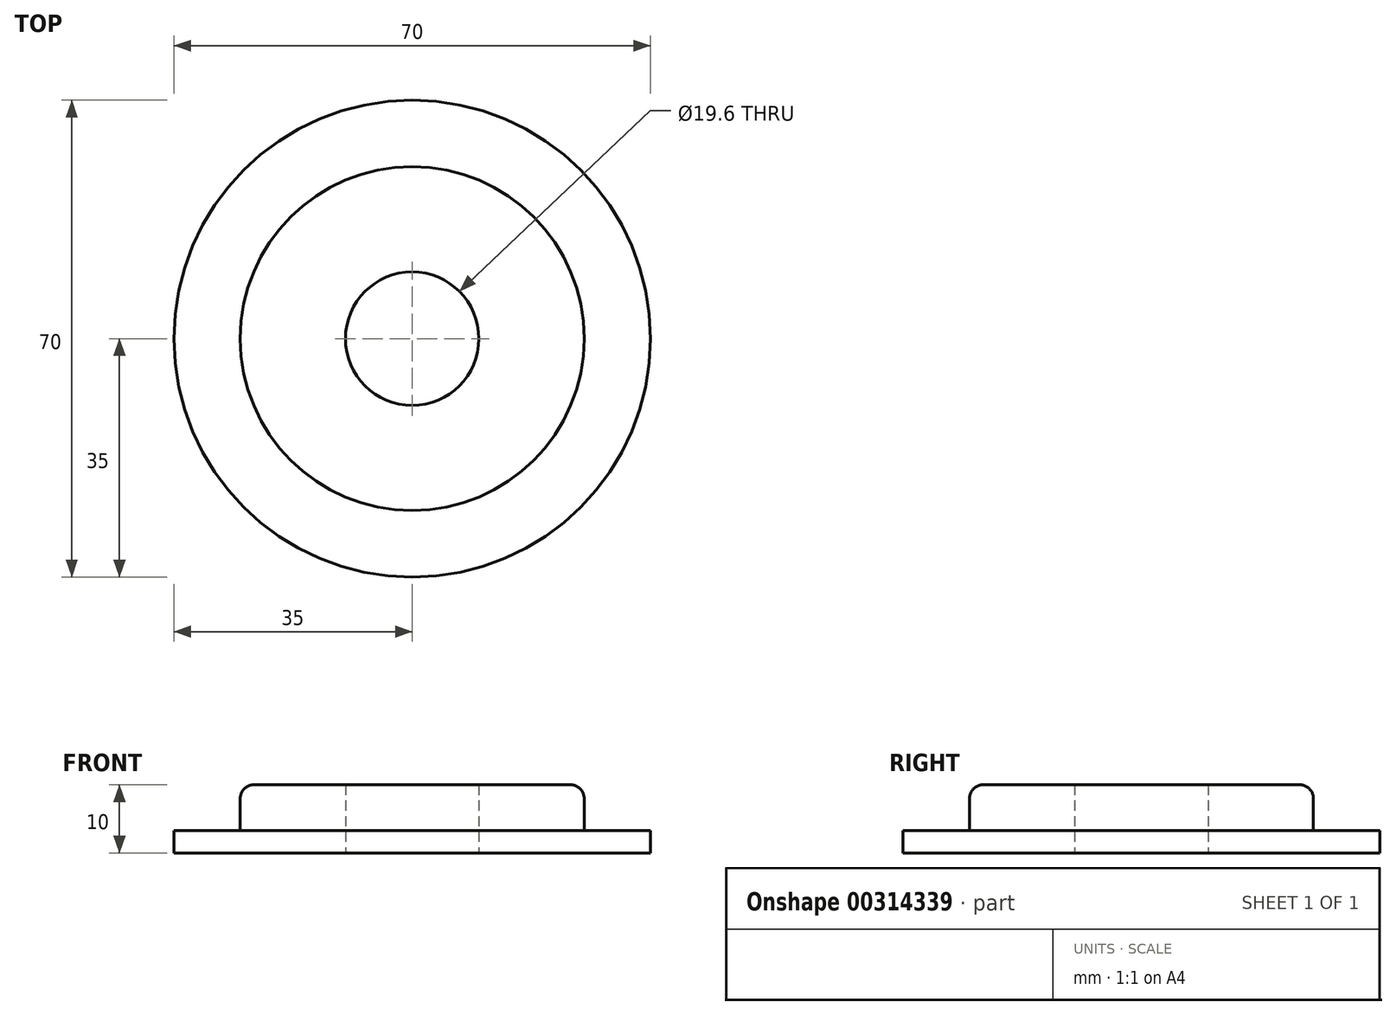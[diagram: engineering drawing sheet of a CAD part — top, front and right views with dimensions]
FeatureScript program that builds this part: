
annotation { "Feature Type Name" : "Feature", "Feature Type Description" : "" }
export const myFeature = defineFeature(function(context is Context, id is Id, definition is map)
    precondition{}
    {
        {
            var Q0;
            Q0=qCreatedBy(makeId("Top.planeOp"),FACE);
            var sketch = newSketch(context, id + "F0", { "sketchPlane" : qUnion([Q0])});
            skCircle(sketch, "E0", {"center": v(0, 0) * mm, "radius": 25.25 * mm});
            skCircle(sketch, "E1", {"center": v(0, 0) * mm, "radius": 9.8 * mm});
            skCircle(sketch, "E2", {"center": v(0, 0) * mm, "radius": 35 * mm});
            skCircle(sketch, "E3", {"center": v(0, 0) * mm, "radius": 12 * mm});
            skCircle(sketch, "E4", {"center": v(0, 0) * mm, "radius": 32 * mm});
            skSolve(sketch);
        }
        {
            var Q0;
            Q0=makeQuery(id+"F0.imprint","IMPRINT",FACE,{"disambiguationData":[TD([[makeQuery(id+"F0.imprint","IMPRINT",EDGE,{"derivedFrom":sQuery(id+"F0.wireOp",EDGE,"E0")}),1.0]])]});
            var Q1;
            Q1=makeQuery(id+"F0.imprint","IMPRINT",FACE,{"disambiguationData":[TD([[makeQuery(id+"F0.imprint","IMPRINT",EDGE,{"derivedFrom":sQuery(id+"F0.wireOp",EDGE,"E1")}),-1.0]])]});
            var Q2;
            {var subQ0=sQuery(id+"F0.wireOp",EDGE,"DjPiPHxe-zXuA-ZsiI-Qa3n-cukn8P3f6TYJ");var subQ1=sQuery(id+"F0.wireOp",EDGE,"E1");var subQ2=makeQuery(id+"F0.imprint","INTERSECT",VERTEX,{"derivedFrom":[subQ1,subQ0]});Q2=makeQuery(id+"F0.imprint","IMPRINT",FACE,{"disambiguationData":[TD([[makeQuery(id+"F0.imprint","IMPRINT",EDGE,{"disambiguationData":[TD([[subQ2,-1.0]])],"derivedFrom":subQ1}),-1.0]])]});}
            var Q3;
            {var subQ0=sQuery(id+"F0.wireOp",EDGE,"a9Ajcc4s-mQx2-FiMb-RlTi-ik9VL1WOjk8D");var subQ1=sQuery(id+"F0.wireOp",EDGE,"E1");var subQ2=makeQuery(id+"F0.imprint","INTERSECT",VERTEX,{"derivedFrom":[subQ1,subQ0]});Q3=makeQuery(id+"F0.imprint","IMPRINT",FACE,{"disambiguationData":[TD([[makeQuery(id+"F0.imprint","IMPRINT",EDGE,{"disambiguationData":[TD([[subQ2,-1.0]])],"derivedFrom":subQ1}),-1.0]])]});}
            extrude(context, id + "F1", {"entities" : qUnion([Q0, Q1, Q2, Q3]), "depth" : 10 * mm});
        }
        {
            var Q0;
            Q0=makeQuery(id+"F0.imprint","IMPRINT",FACE,{"disambiguationData":[TD([[makeQuery(id+"F0.imprint","IMPRINT",EDGE,{"derivedFrom":sQuery(id+"F0.wireOp",EDGE,"E0")}),-1.0]])]});
            var Q1;
            {var subQ0=sQuery(id+"F0.wireOp",EDGE,"a9Ajcc4s-mQx2-FiMb-RlTi-ik9VL1WOjk8D");var subQ1=sQuery(id+"F0.wireOp",EDGE,"E2");var subQ2=makeQuery(id+"F0.imprint","INTERSECT",VERTEX,{"derivedFrom":[subQ1,subQ0]});Q1=makeQuery(id+"F0.imprint","IMPRINT",FACE,{"disambiguationData":[TD([[makeQuery(id+"F0.imprint","IMPRINT",EDGE,{"disambiguationData":[TD([[subQ2,1.0]])],"derivedFrom":subQ1}),1.0]])]});}
            var Q2;
            {var subQ0=sQuery(id+"F0.wireOp",EDGE,"mODTY8X1-IRk4-EtVv-bdWa-POD7j5AjUbJf");var subQ1=sQuery(id+"F0.wireOp",EDGE,"E2");var subQ2=makeQuery(id+"F0.imprint","INTERSECT",VERTEX,{"derivedFrom":[subQ1,subQ0]});Q2=makeQuery(id+"F0.imprint","IMPRINT",FACE,{"disambiguationData":[TD([[makeQuery(id+"F0.imprint","IMPRINT",EDGE,{"disambiguationData":[TD([[subQ2,1.0]])],"derivedFrom":subQ1}),1.0]])]});}
            var Q3;
            {var subQ0=sQuery(id+"F0.wireOp",EDGE,"a9Ajcc4s-mQx2-FiMb-RlTi-ik9VL1WOjk8D");var subQ1=sQuery(id+"F0.wireOp",EDGE,"E2");var subQ2=makeQuery(id+"F0.imprint","INTERSECT",VERTEX,{"derivedFrom":[subQ1,subQ0]});Q3=makeQuery(id+"F0.imprint","IMPRINT",FACE,{"disambiguationData":[TD([[makeQuery(id+"F0.imprint","IMPRINT",EDGE,{"disambiguationData":[TD([[subQ2,-1.0]])],"derivedFrom":subQ1}),1.0]])]});}
            var Q4;
            {var subQ0=sQuery(id+"F0.wireOp",EDGE,"mODTY8X1-IRk4-EtVv-bdWa-POD7j5AjUbJf");var subQ1=sQuery(id+"F0.wireOp",EDGE,"E2");var subQ2=makeQuery(id+"F0.imprint","INTERSECT",VERTEX,{"derivedFrom":[subQ1,subQ0]});Q4=makeQuery(id+"F0.imprint","IMPRINT",FACE,{"disambiguationData":[TD([[makeQuery(id+"F0.imprint","IMPRINT",EDGE,{"disambiguationData":[TD([[subQ2,-1.0]])],"derivedFrom":subQ1}),1.0]])]});}
            extrude(context, id + "F2", {"entities" : qUnion([Q0, Q1, Q2, Q3, Q4]), "operationType" : NewBodyOperationType.ADD, "depth" : 3.25 * mm});
        }
        {
            var Q0;
            Q0=makeQuery(id+"F1.opExtrude","CAP_EDGE",EDGE,{"disambiguationData":[OSD([sQuery(id+"F0.wireOp",EDGE,"E0")])],"isStart":false});
            fillet(context, id + "F3", {"entities" : qUnion([Q0]), "radius" : 2 * mm, "tangentPropagation" : true, "allowEdgeOverflow" : false});
        }
    });
